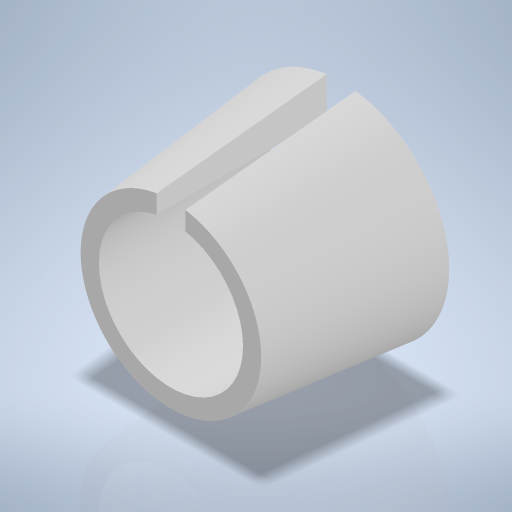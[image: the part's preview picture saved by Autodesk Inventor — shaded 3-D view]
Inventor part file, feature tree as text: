
AUTODESK INVENTOR PART (.ipt)
format: ipt  version: 2024 (Build 280153000, 153)  size: 243,200 bytes
history: native  units: mm
features: sketch x3, extrude x2, other x1, hole x1
ambient origin geometry x8: Origin, YZ Plane, XZ Plane, XY Plane, X Axis, Y Axis, Z Axis, Center Point
bodies: Volumenkörper1 (feature_tree)
feature tree (7):
  extrude  "Extrusion1"  Depth=11.8mm TaperAngle=0.0deg
  other  "Flächenverjüngung1"
  hole  "Bohrung1"  [1 undecoded]
  extrude  "Extrusion2"  Depth=2.0mm TaperAngle=0.0deg
  sketch  "Skizze1"  dims[d0=15.0mm d1=11.8mm d2=0.0mm]
  sketch  "Skizze2"  dims[d3=1.047198mm]
  sketch  "Skizze4"  dims[d4=10.0mm d5=6.0mm d6=4.0mm d7=2.0mm d8=90.0deg d9=8.0mm d10=0.0mm d12=2.0mm d13=11.8mm d14=0.0mm]
note: 1 required parameter value undecoded (feature->parameter linkage not recoverable at this tier; creation-order binding heuristic only, values carry confidence <= 0.55)
